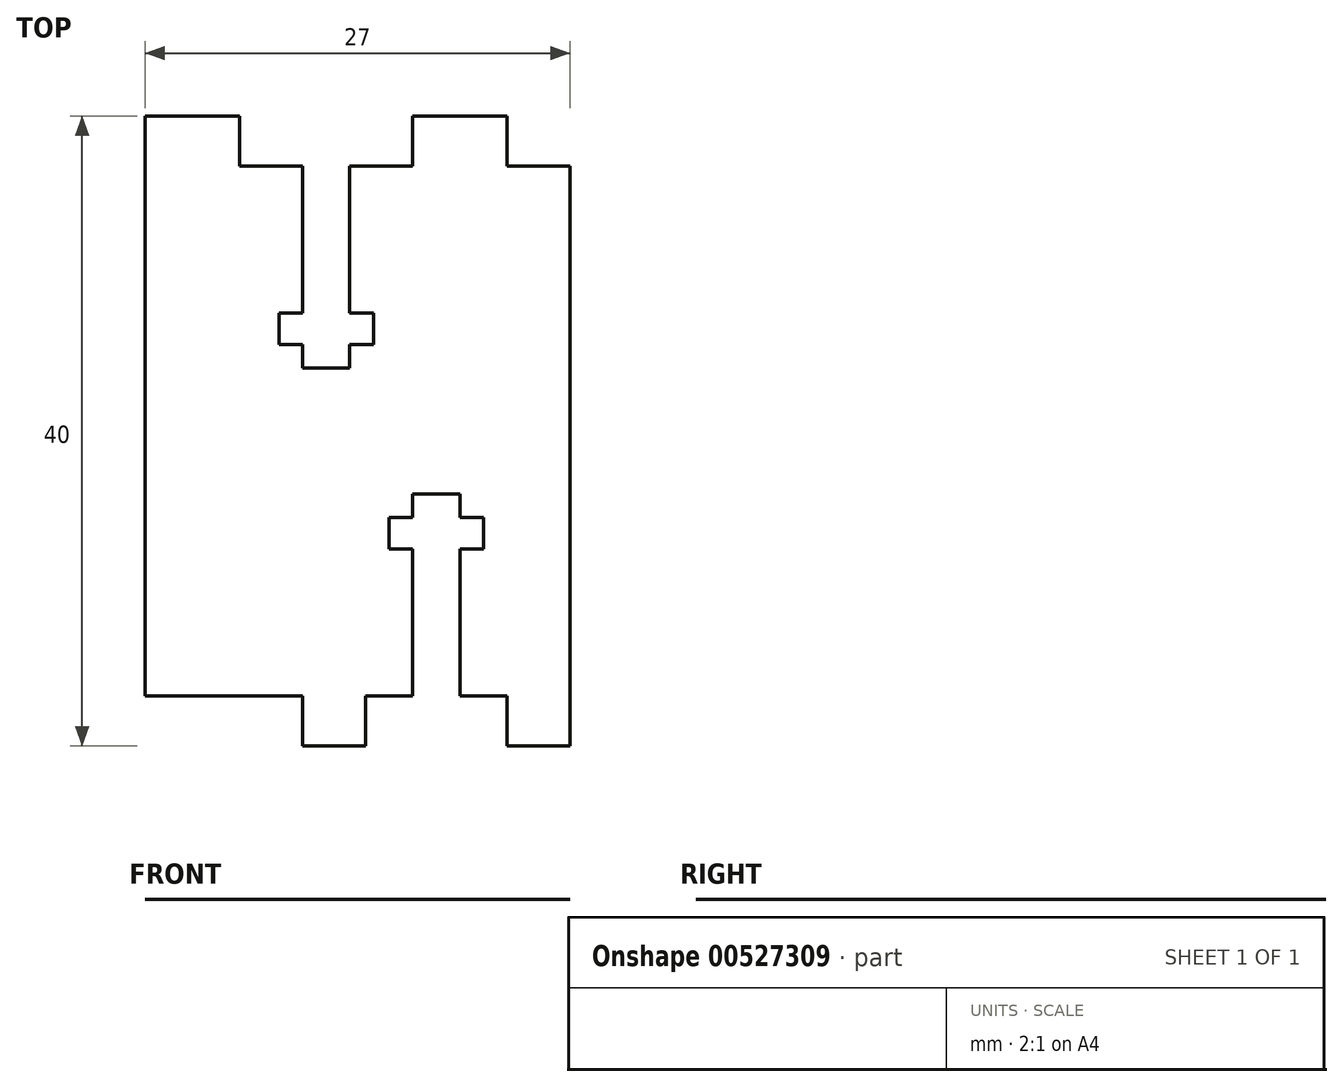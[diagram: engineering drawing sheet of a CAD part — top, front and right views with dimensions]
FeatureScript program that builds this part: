
annotation { "Feature Type Name" : "Feature", "Feature Type Description" : "" }
export const myFeature = defineFeature(function(context is Context, id is Id, definition is map)
    precondition{}
    {
        {
            var Q0;
            Q0=qCreatedBy(makeId("Top.planeOp"),FACE);
            var sketch = newSketch(context, id + "F0", { "sketchPlane" : qUnion([Q0])});
            skLineSegment(sketch, "E0.bottom", {"start": v(-26.61, 30.22) * mm, "end": v(-23.61, 30.22) * mm});
            skLineSegment(sketch, "E0.top", {"start": v(-26.61, 14.22) * mm, "end": v(-23.61, 14.22) * mm});
            skLineSegment(sketch, "E0.left", {"start": v(-26.61, 30.22) * mm, "end": v(-26.61, 14.22) * mm});
            skLineSegment(sketch, "E0.right", {"start": v(-23.61, 30.22) * mm, "end": v(-23.61, 14.22) * mm});
            skPoint(sketch, "E0.middle", {"position": v(-25.11, 22.22) * mm});
            skLineSegment(sketch, "E1.bottom", {"start": v(-28.11, 17.72) * mm, "end": v(-22.11, 17.72) * mm});
            skLineSegment(sketch, "E1.top", {"start": v(-28.11, 15.72) * mm, "end": v(-22.11, 15.72) * mm});
            skLineSegment(sketch, "E1.left", {"start": v(-28.11, 17.72) * mm, "end": v(-28.11, 15.72) * mm});
            skLineSegment(sketch, "E1.right", {"start": v(-22.11, 17.72) * mm, "end": v(-22.11, 15.72) * mm});
            skPoint(sketch, "E1.middle", {"position": v(-25.11, 16.72) * mm});
            skLineSegment(sketch, "E2", {"start": v(-25.11, 22.22) * mm, "end": v(-25.11, 16.72) * mm});
            skLineSegment(sketch, "E3.bottom", {"start": v(-19.61, 30.22) * mm, "end": v(-13.61, 30.22) * mm});
            skLineSegment(sketch, "E3.top", {"start": v(-19.61, 27.05) * mm, "end": v(-13.61, 27.05) * mm});
            skLineSegment(sketch, "E3.left", {"start": v(-19.61, 30.22) * mm, "end": v(-19.61, 27.05) * mm});
            skLineSegment(sketch, "E3.right", {"start": v(-13.61, 30.22) * mm, "end": v(-13.61, 27.05) * mm});
            skLineSegment(sketch, "E4.MirrorCS", {"start": v(-30.61, 30.22) * mm, "end": v(-30.61, 27.05) * mm});
            skLineSegment(sketch, "E5.MirrorCS", {"start": v(-30.61, 30.22) * mm, "end": v(-36.61, 30.22) * mm});
            skLineSegment(sketch, "E6.MirrorCS", {"start": v(-36.61, 30.22) * mm, "end": v(-36.61, 27.05) * mm});
            skLineSegment(sketch, "E7.MirrorCS", {"start": v(-30.61, 27.05) * mm, "end": v(-36.61, 27.05) * mm});
            skLineSegment(sketch, "E8.bottom", {"start": v(-19.61, 6.22) * mm, "end": v(-16.61, 6.22) * mm});
            skLineSegment(sketch, "E8.top", {"start": v(-19.61, -9.78) * mm, "end": v(-16.61, -9.78) * mm});
            skLineSegment(sketch, "E8.left", {"start": v(-19.61, 6.22) * mm, "end": v(-19.61, -9.78) * mm});
            skLineSegment(sketch, "E8.right", {"start": v(-16.61, 6.22) * mm, "end": v(-16.61, -9.78) * mm});
            skPoint(sketch, "E8.middle", {"position": v(-18.11, -1.78) * mm});
            skLineSegment(sketch, "E9.bottom", {"start": v(-21.11, 2.72) * mm, "end": v(-15.11, 2.72) * mm});
            skLineSegment(sketch, "E9.top", {"start": v(-21.11, 4.72) * mm, "end": v(-15.11, 4.72) * mm});
            skLineSegment(sketch, "E9.left", {"start": v(-21.11, 2.72) * mm, "end": v(-21.11, 4.72) * mm});
            skLineSegment(sketch, "E9.right", {"start": v(-15.11, 2.72) * mm, "end": v(-15.11, 4.72) * mm});
            skPoint(sketch, "E9.middle", {"position": v(-18.11, 3.72) * mm});
            skLineSegment(sketch, "E10", {"start": v(-18.11, 3.72) * mm, "end": v(-18.11, -1.78) * mm});
            skLineSegment(sketch, "E11.bottom", {"start": v(-22.61, -9.78) * mm, "end": v(-26.61, -9.78) * mm});
            skLineSegment(sketch, "E11.top", {"start": v(-22.61, -6.6) * mm, "end": v(-26.61, -6.6) * mm});
            skLineSegment(sketch, "E11.left", {"start": v(-22.61, -9.78) * mm, "end": v(-22.61, -6.6) * mm});
            skLineSegment(sketch, "E11.right", {"start": v(-26.61, -9.78) * mm, "end": v(-26.61, -6.6) * mm});
            skLineSegment(sketch, "E12.MirrorCS", {"start": v(-13.61, -6.6) * mm, "end": v(-9.61, -6.6) * mm});
            skLineSegment(sketch, "E13.MirrorCS", {"start": v(-13.61, -9.78) * mm, "end": v(-13.61, -6.6) * mm});
            skLineSegment(sketch, "E14.MirrorCS", {"start": v(-13.61, -9.78) * mm, "end": v(-9.61, -9.78) * mm});
            skLineSegment(sketch, "E15.MirrorCS", {"start": v(-9.61, -9.78) * mm, "end": v(-9.61, -6.6) * mm});
            skLineSegment(sketch, "E16.bottom", {"start": v(-36.61, 30.22) * mm, "end": v(-9.61, 30.22) * mm});
            skLineSegment(sketch, "E16.top", {"start": v(-36.61, -9.78) * mm, "end": v(-9.61, -9.78) * mm});
            skLineSegment(sketch, "E16.left", {"start": v(-36.61, 30.22) * mm, "end": v(-36.61, -9.78) * mm});
            skLineSegment(sketch, "E16.right", {"start": v(-9.61, 30.22) * mm, "end": v(-9.61, -9.78) * mm});
            skLineSegment(sketch, "E17", {"start": v(-30.61, 27.05) * mm, "end": v(-19.61, 27.05) * mm});
            skLineSegment(sketch, "E18", {"start": v(-13.61, 27.05) * mm, "end": v(-9.61, 27.05) * mm});
            skLineSegment(sketch, "E19", {"start": v(-13.61, -6.6) * mm, "end": v(-22.61, -6.6) * mm});
            skLineSegment(sketch, "E20", {"start": v(-26.61, -6.6) * mm, "end": v(-36.61, -6.6) * mm});
            skSolve(sketch);
        }
        {
            var Q0;
            {var subQ23=sQuery(id+"F0.wireOp",EDGE,"E0.top");Q0=makeQuery(id+"F0.imprint","IMPRINT",FACE,{"disambiguationData":[TD([[makeQuery(id+"F0.imprint","IMPRINT",EDGE,{"derivedFrom":subQ23}),-1.0]])]});}
            var Q1;
            {var subQ0=sQuery(id+"F0.wireOp",EDGE,"E4.MirrorCS");Q1=makeQuery(id+"F0.imprint","IMPRINT",FACE,{"disambiguationData":[TD([[makeQuery(id+"F0.imprint","IMPRINT",EDGE,{"derivedFrom":subQ0}),-1.0]])]});}
            var Q2;
            Q2=makeQuery(id+"F0.imprint","IMPRINT",FACE,{"disambiguationData":[TD([[makeQuery(id+"F0.imprint","IMPRINT",EDGE,{"derivedFrom":sQuery(id+"F0.wireOp",EDGE,"E3.top")}),1.0]])]});
            var Q3;
            Q3=makeQuery(id+"F0.imprint","IMPRINT",FACE,{"disambiguationData":[TD([[makeQuery(id+"F0.imprint","IMPRINT",EDGE,{"derivedFrom":sQuery(id+"F0.wireOp",EDGE,"E11.top")}),1.0]])]});
            var Q4;
            {var subQ0=sQuery(id+"F0.wireOp",EDGE,"E12.MirrorCS");Q4=makeQuery(id+"F0.imprint","IMPRINT",FACE,{"disambiguationData":[TD([[makeQuery(id+"F0.imprint","IMPRINT",EDGE,{"derivedFrom":subQ0}),-1.0]])]});}
            extrude(context, id + "F1", {"entities" : qUnion([Q0, Q1, Q2, Q3, Q4]), "depth" : 1 / 203.2 * mm, "offsetDistance" : 25 * mm});
        }
    });
